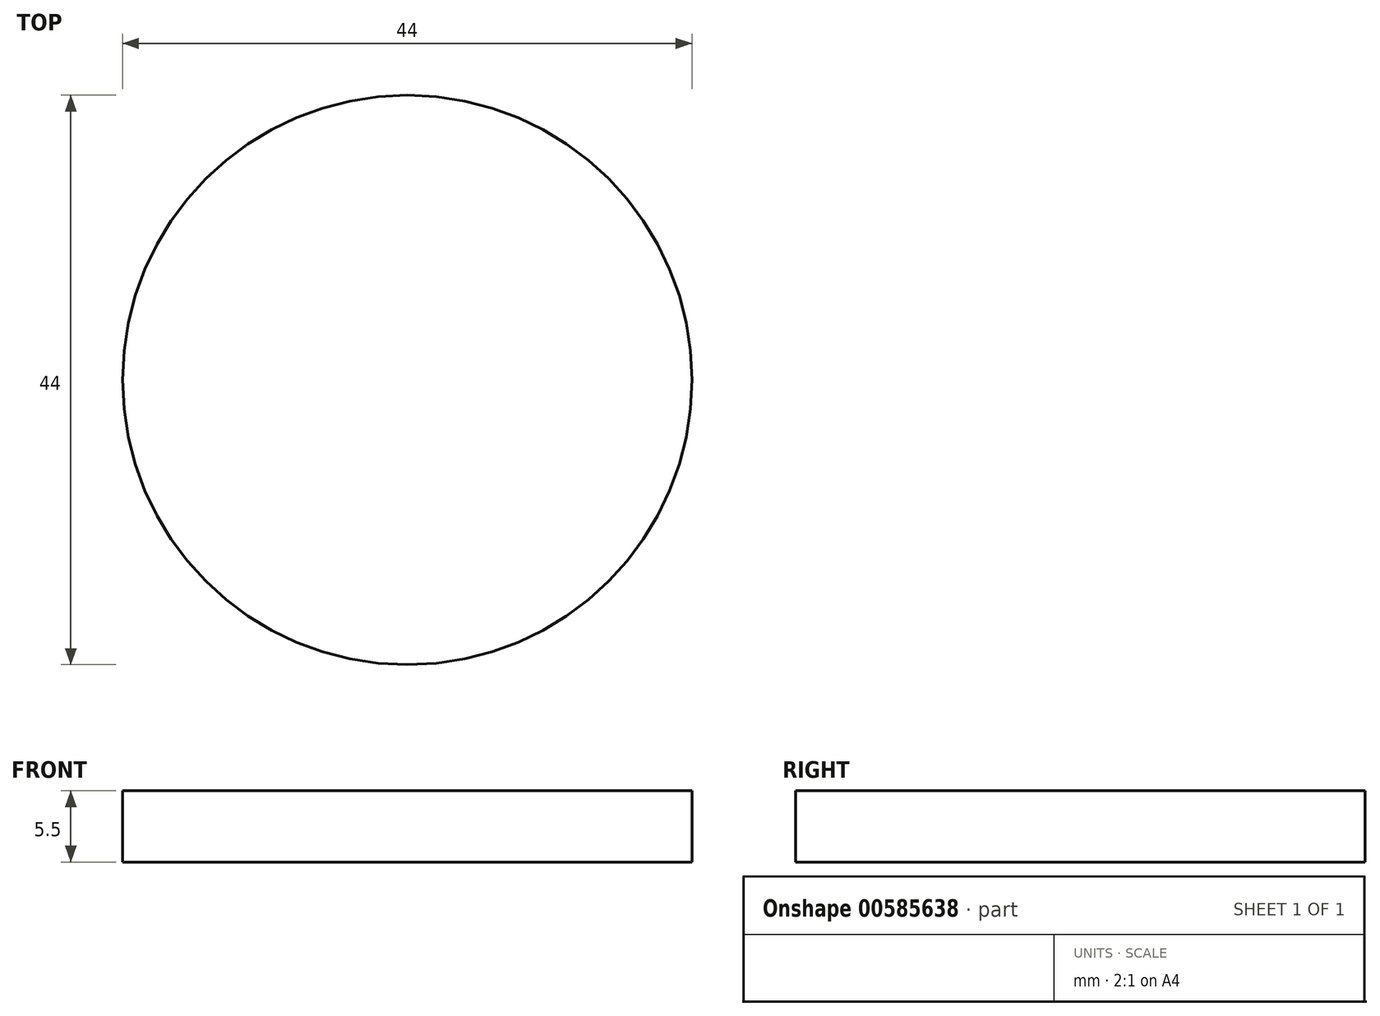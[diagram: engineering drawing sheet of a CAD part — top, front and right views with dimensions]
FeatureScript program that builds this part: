
annotation { "Feature Type Name" : "Feature", "Feature Type Description" : "" }
export const myFeature = defineFeature(function(context is Context, id is Id, definition is map)
    precondition{}
    {
        {
            var Q0;
            Q0=qCreatedBy(makeId("Top.planeOp"),FACE);
            var sketch = newSketch(context, id + "F0", { "sketchPlane" : qUnion([Q0])});
            skCircle(sketch, "E0", {"center": v(0, 0) * mm, "radius": 22 * mm});
            skSolve(sketch);
        }
        {
            var Q0;
            Q0=makeQuery(id+"F0.imprint","IMPRINT",FACE,{"disambiguationData":[TD([[makeQuery(id+"F0.imprint","IMPRINT",EDGE,{"derivedFrom":sQuery(id+"F0.wireOp",EDGE,"E0")}),1.0]])]});
            extrude(context, id + "F1", {"entities" : qUnion([Q0]), "oppositeDirection" : true, "depth" : 5.5 * mm, "offsetDistance" : 25 * mm});
        }
    });
